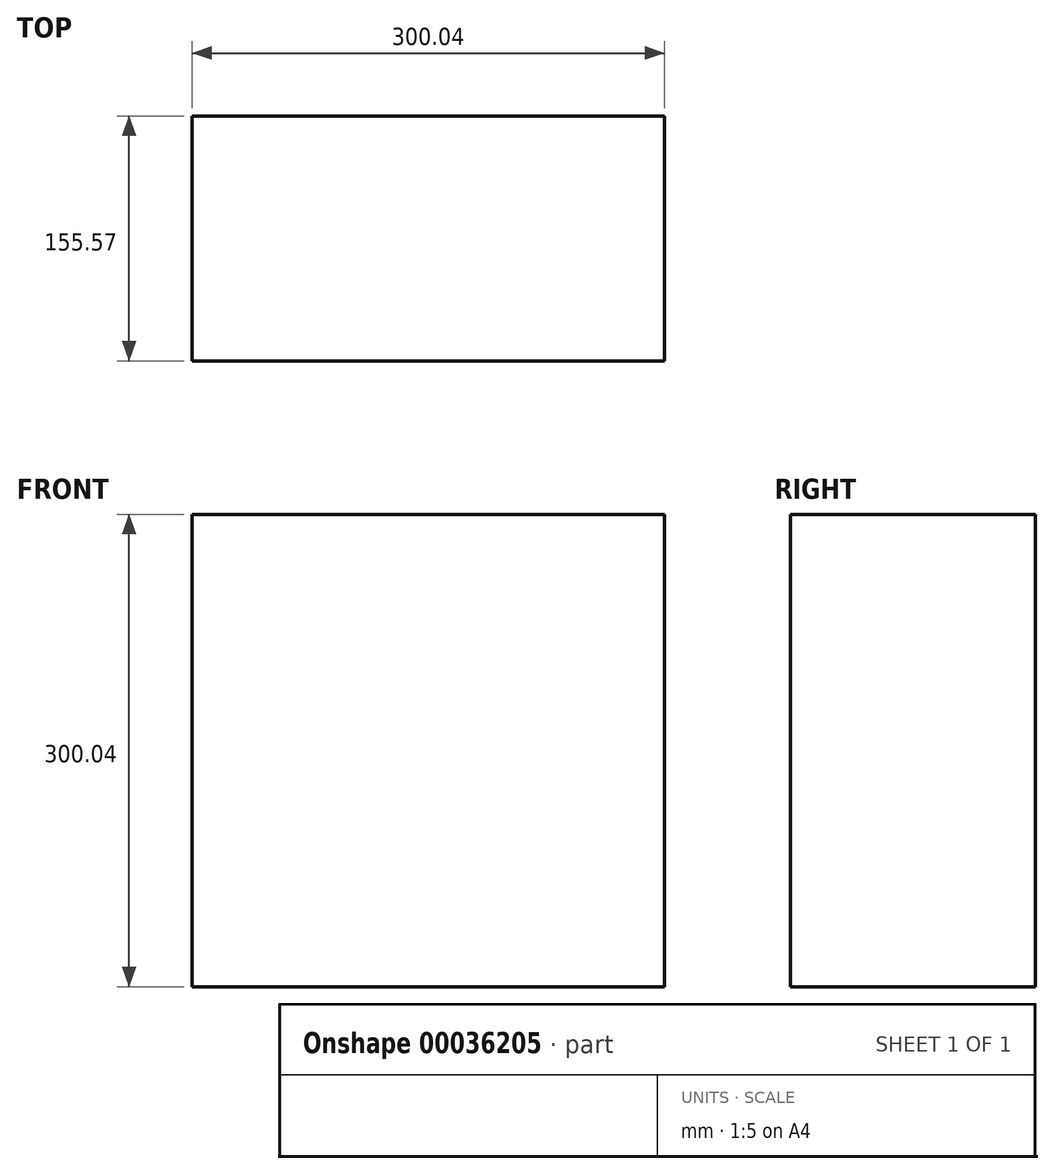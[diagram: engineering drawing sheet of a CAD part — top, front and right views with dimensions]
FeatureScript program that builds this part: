
annotation { "Feature Type Name" : "Feature", "Feature Type Description" : "" }
export const myFeature = defineFeature(function(context is Context, id is Id, definition is map)
    precondition{}
    {
        {
            var Q0;
            Q0=qCreatedBy(makeId("Front.planeOp"),FACE);
            var sketch = newSketch(context, id + "F0", { "sketchPlane" : qUnion([Q0])});
            skLineSegment(sketch, "E0.bottom", {"start": v(0, 0) * mm, "end": v(300.04, 0) * mm});
            skLineSegment(sketch, "E0.top", {"start": v(0, 300.04) * mm, "end": v(300.04, 300.04) * mm});
            skLineSegment(sketch, "E0.left", {"start": v(0, 0) * mm, "end": v(0, 300.04) * mm});
            skLineSegment(sketch, "E0.right", {"start": v(300.04, 0) * mm, "end": v(300.04, 300.04) * mm});
            skSolve(sketch);
        }
        {
            var Q0;
            Q0 = qSketchRegion(id + "F0", true);
            extrude(context, id + "F1", {"entities" : qUnion([Q0]), "depth" : 155.57 * mm});
        }
    });
